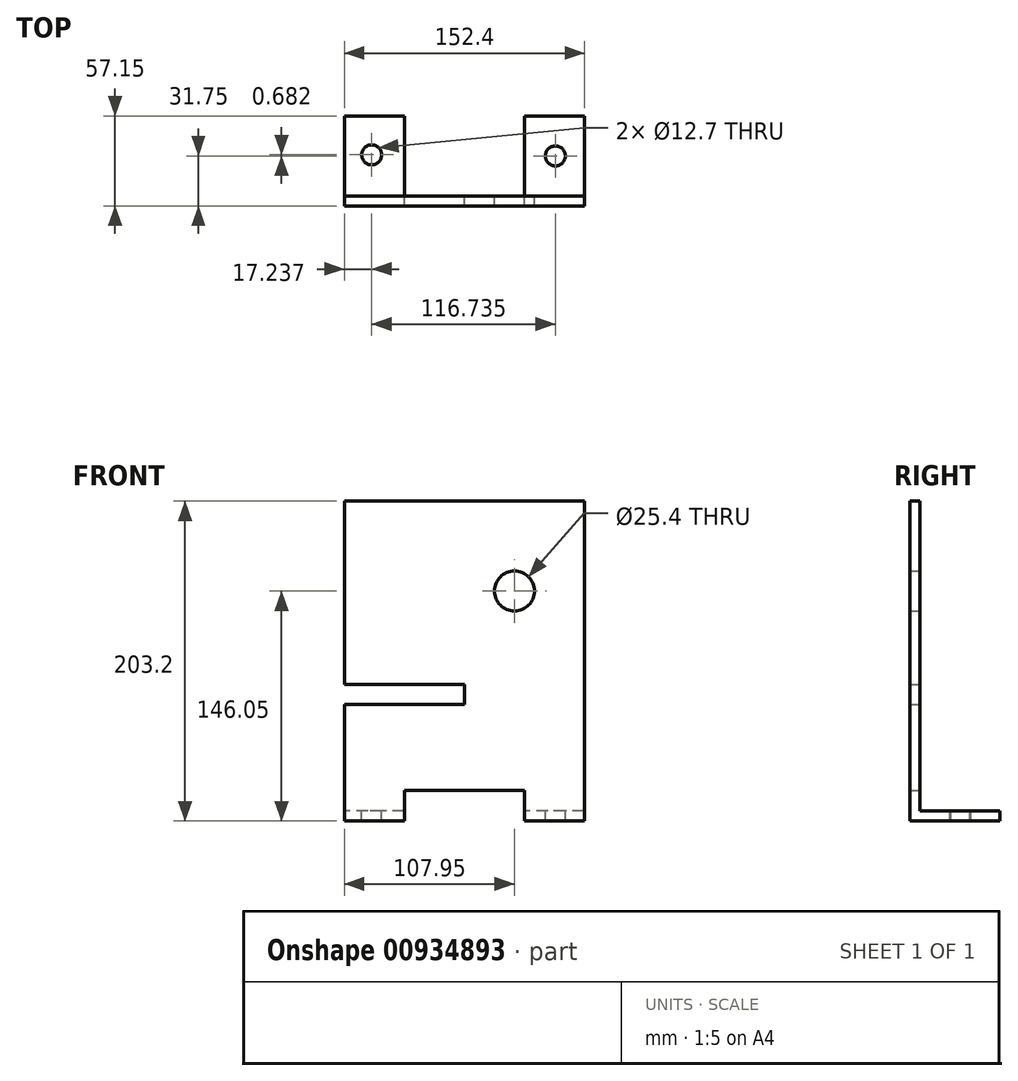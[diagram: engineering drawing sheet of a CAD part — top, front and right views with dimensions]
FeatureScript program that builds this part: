
annotation { "Feature Type Name" : "Feature", "Feature Type Description" : "" }
export const myFeature = defineFeature(function(context is Context, id is Id, definition is map)
    precondition{}
    {
        {
            var Q0;
            Q0=qCreatedBy(makeId("Front.planeOp"),FACE);
            var sketch = newSketch(context, id + "F0", { "sketchPlane" : qUnion([Q0])});
            skCircle(sketch, "E0", {"center": v(0, 0) * mm, "radius": 12.7 * mm});
            skLineSegment(sketch, "E1", {"start": v(-107.95, 57.15) * mm, "end": v(44.45, 57.15) * mm});
            skLineSegment(sketch, "E2", {"start": v(44.45, 57.15) * mm, "end": v(44.45, -146.05) * mm});
            skLineSegment(sketch, "E3", {"start": v(44.45, -146.05) * mm, "end": v(6.35, -146.05) * mm});
            skLineSegment(sketch, "E4", {"start": v(6.35, -146.05) * mm, "end": v(6.35, -126.62) * mm});
            skLineSegment(sketch, "E5", {"start": v(6.35, -126.62) * mm, "end": v(-69.85, -126.62) * mm});
            skLineSegment(sketch, "E6", {"start": v(-69.85, -126.62) * mm, "end": v(-69.85, -146.05) * mm});
            skLineSegment(sketch, "E7", {"start": v(-69.85, -146.05) * mm, "end": v(-107.95, -146.05) * mm});
            skLineSegment(sketch, "E8", {"start": v(-107.95, -146.05) * mm, "end": v(-107.95, -72.09) * mm});
            skLineSegment(sketch, "E9", {"start": v(-107.95, -72.09) * mm, "end": v(-31.62, -72.09) * mm});
            skLineSegment(sketch, "E10", {"start": v(-31.62, -72.09) * mm, "end": v(-31.62, -59.16) * mm});
            skLineSegment(sketch, "E11", {"start": v(-31.62, -59.16) * mm, "end": v(-107.95, -59.16) * mm});
            skLineSegment(sketch, "E12", {"start": v(-107.95, -59.16) * mm, "end": v(-107.95, 57.15) * mm});
            skSolve(sketch);
        }
        {
            var Q0;
            Q0 = qSketchRegion(id + "F0", true);
            extrude(context, id + "F1", {"entities" : qUnion([Q0]), "depth" : 6.35 * mm, "offsetDistance" : 25.4 * mm});
        }
        {
            var Q0;
            Q0=makeQuery(id+"F1.opExtrude","CAP_FACE",FACE,{"disambiguationData":[OSD([sQuery(id+"F0.wireOp",EDGE,"E0"),sQuery(id+"F0.wireOp",EDGE,"E1"),sQuery(id+"F0.wireOp",EDGE,"E2"),sQuery(id+"F0.wireOp",EDGE,"E3"),sQuery(id+"F0.wireOp",EDGE,"E4"),sQuery(id+"F0.wireOp",EDGE,"E5"),sQuery(id+"F0.wireOp",EDGE,"E6"),sQuery(id+"F0.wireOp",EDGE,"E7"),sQuery(id+"F0.wireOp",EDGE,"E8"),sQuery(id+"F0.wireOp",EDGE,"E9"),sQuery(id+"F0.wireOp",EDGE,"E10"),sQuery(id+"F0.wireOp",EDGE,"E11"),sQuery(id+"F0.wireOp",EDGE,"E12")])],"isStart":true});
            var sketch = newSketch(context, id + "F2", { "sketchPlane" : qUnion([Q0])});
            skLineSegment(sketch, "E13", {"start": v(-44.45, -139.7) * mm, "end": v(-6.35, -139.7) * mm});
            skLineSegment(sketch, "E14", {"start": v(69.85, -139.7) * mm, "end": v(107.95, -139.7) * mm});
            skSolve(sketch);
        }
        {
            var Q0;
            Q0 = qSketchRegion(id + "F2", true);
            var Q1;
            {var subQ0=sQuery(id+"F2.wireOp",EDGE,"E13");Q1=makeQuery(id+"F2.imprint","IMPRINT",FACE,{"disambiguationData":[TD([[makeQuery(id+"F2.imprint","IMPRINT",EDGE,{"derivedFrom":subQ0}),-1.0]])]});}
            var Q2;
            {var subQ0=sQuery(id+"F2.wireOp",EDGE,"E14");Q2=makeQuery(id+"F2.imprint","IMPRINT",FACE,{"disambiguationData":[TD([[makeQuery(id+"F2.imprint","IMPRINT",EDGE,{"derivedFrom":subQ0}),-1.0]])]});}
            extrude(context, id + "F3", {"entities" : qUnion([Q0, Q1, Q2]), "operationType" : NewBodyOperationType.ADD, "depth" : 50.8 * mm, "offsetDistance" : 25.4 * mm});
        }
        {
            var Q0;
            Q0=makeQuery(id+"F3.opExtrude","SWEPT_FACE",FACE,{"disambiguationData":[OSD([sQuery(id+"F2.wireOp",EDGE,"E13")])]});
            var sketch = newSketch(context, id + "F4", { "sketchPlane" : qUnion([Q0])});
            skCircle(sketch, "E15", {"center": v(26.02, 25.4) * mm, "radius": 6.35 * mm});
            skPoint(sketch, "E15.centerSnap0", {"position": v(44.45, 25.4) * mm});
            skCircle(sketch, "E16", {"center": v(-90.71, 26.08) * mm, "radius": 6.35 * mm});
            skSolve(sketch);
        }
        {
            var Q0;
            Q0 = qSketchRegion(id + "F4", true);
            extrude(context, id + "F5", {"entities" : qUnion([Q0]), "operationType" : NewBodyOperationType.REMOVE, "oppositeDirection" : true, "depth" : 25.4 * mm, "offsetDistance" : 25.4 * mm});
        }
    });
